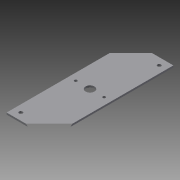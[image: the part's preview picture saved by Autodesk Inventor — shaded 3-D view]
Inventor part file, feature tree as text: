
AUTODESK INVENTOR PART (.ipt)
format: ipt  version: 2015 SP1 (Build 190203100, 203)  size: 103,424 bytes
history: native  units: in
note: dims shown in document units (in); Inventor stores cm internally (conversion verified against a paired STEP export)
features: sketch x3, extrude x2, hole x1
ambient origin geometry x8: Origin, YZ Plane, XZ Plane, XY Plane, X Axis, Y Axis, Z Axis, Center Point
bodies: Solid1 (feature_tree)
feature tree (6):
  extrude  "Extrusion1"  Depth=8.75in
  extrude  "Extrusion2"  Depth=0.125in
  hole  "Hole1"  [1 undecoded]
  sketch  "Sketch1"  dims[d0=3.0in d1=8.75in]
  sketch  "Sketch2"  dims[d2=0.125in d3=0.0in d4=4.375in]
  sketch  "Sketch3"  dims[d5=1.5in d6=1.0in d7=1.0in d8=4.375in d9=4.375in d10=0.2in d11=0.2in d12=0.625in d13=1.0in d14=0.0in d15=0.5in d16=0.5in d17=0.5in d18=0.5in d19=0.5in d20=0.5in d21=0.5in d22=0.5in d23=0.25in d24=0.75in d25=0.375in d26=0.25in d27=0.5635in d28=1.0in d29=0.8108in]
note: 1 required parameter value undecoded (feature->parameter linkage not recoverable at this tier; creation-order binding heuristic only, values carry confidence <= 0.55)
